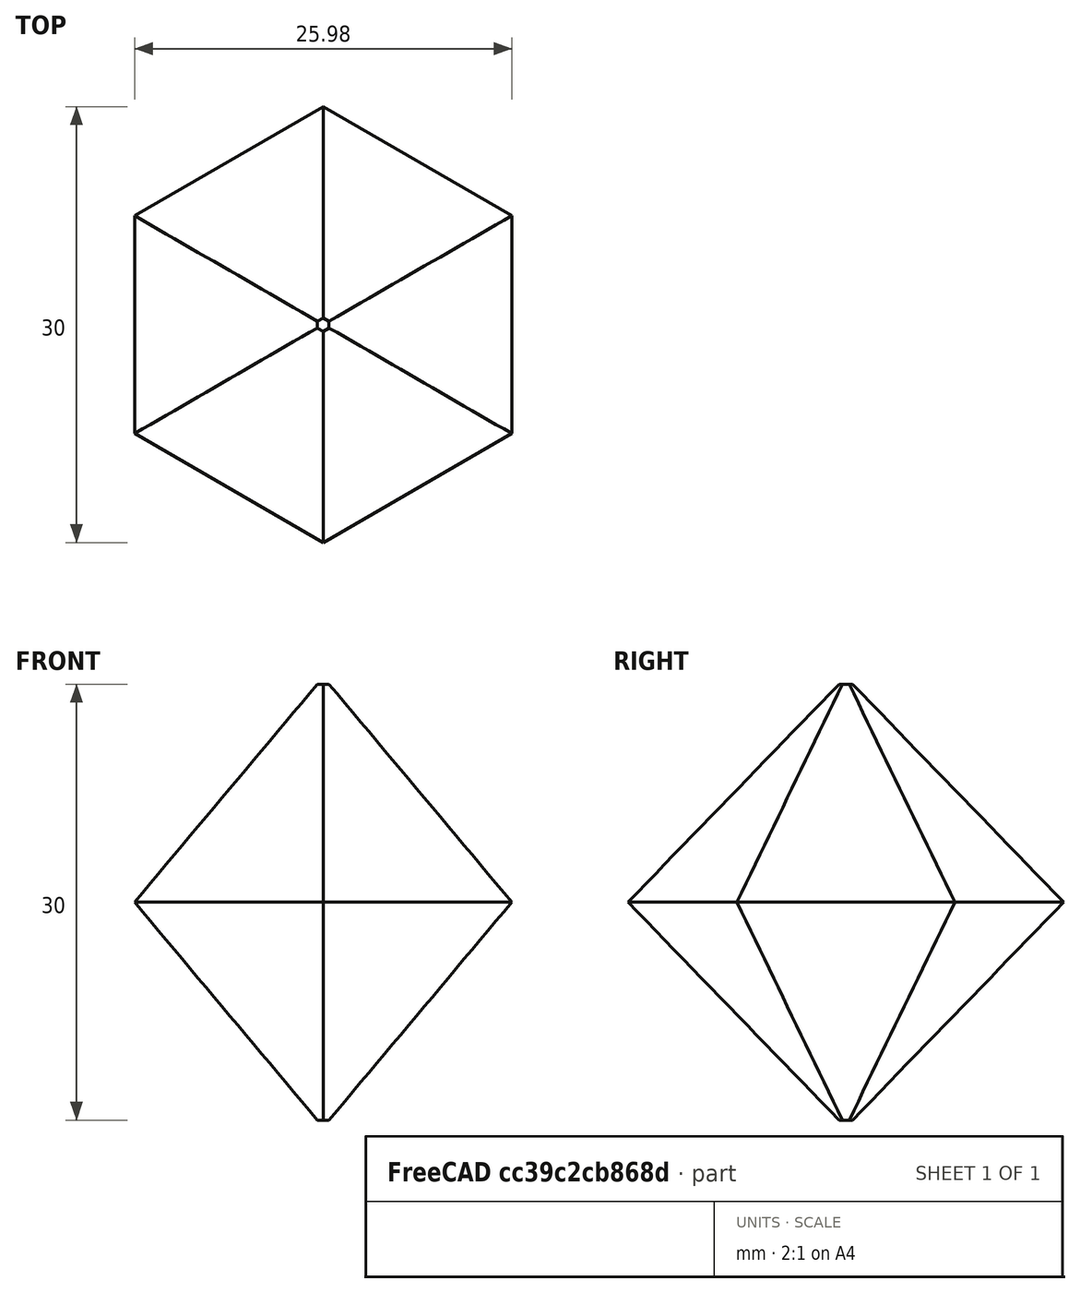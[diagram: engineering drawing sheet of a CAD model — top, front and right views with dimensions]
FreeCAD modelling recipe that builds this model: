
FCSTD DOCUMENT  (FreeCAD 1.1R20260414 (Git shallow))
Label: lesson17
License: All rights reserved
objects: App::Point×1, Sketcher::SketchObject×1, PartDesign::Pad×1, PartDesign::Body×1, App::VarSet×1
note: 6 computed .brp shape members not serialized (recipe doc carries the construction recipe); baked Part::Feature solids carry a one-line shape summary decoded from their .brp

FEATURE [App::Point] Origin001
  Role = Origin
FEATURE [Sketcher::SketchObject] Sketch
  ArcFitTolerance = 1e-06
  AttachmentSupport = -> [Origin]
  ExternalTypes = [0]
  FullyConstrained = true
  MakeInternals = false
  MapMode = 5
  _ExternalGeoVersion = 1
  sketch-geometry (7):
    g0: LineSegment StartX=0 StartY=-15 StartZ=0 EndX=12.9904 EndY=-7.5 EndZ=0
    g1: LineSegment StartX=12.9904 StartY=-7.5 StartZ=0 EndX=12.9904 EndY=7.5 EndZ=0
    g2: LineSegment StartX=12.9904 StartY=7.5 StartZ=0 EndX=-6e-16 EndY=15 EndZ=0
    g3: LineSegment StartX=-6e-16 StartY=15 StartZ=0 EndX=-12.9904 EndY=7.5 EndZ=0
    g4: LineSegment StartX=-12.9904 StartY=7.5 StartZ=0 EndX=-12.9904 EndY=-7.5 EndZ=0
    g5: LineSegment StartX=-12.9904 StartY=-7.5 StartZ=0 EndX=6e-16 EndY=-15 EndZ=0
    g6: Circle [constr] CenterX=0 CenterY=0 CenterZ=0 NormalX=0 NormalY=0 NormalZ=1 AngleXU=0 Radius=15
  constraints (16):
    c: Coincident(g0,g1)
    c: Coincident(g1,g2)
    c: Coincident(g2,g3)
    c: Coincident(g3,g4)
    c: Coincident(g4,g5)
    c: Coincident(g5,g0)
    c: Equal(g0, g1-g5) x5
    c: PointOnObject(g0,g6)
    c: PointOnObject(g1,g6)
    c: PointOnObject(g2,g6)
    c: PointOnObject(g3,g6)
    c: PointOnObject(g4,g6)
    c: PointOnObject(g5,g6)
    c: Coincident(g6,g-1)
    c: PointOnObject(g5,g-2)
    c: Diameter(g6) = 30
FEATURE [PartDesign::Pad] Pad
  Direction = (0,0,1)
  Length = 30
  Length2 = 10
  Profile = -> Sketch
  ReferenceAxis = -> Sketch [N_Axis]
  Refine = true
  SideType = 2
  Suppressed = false
  TaperAngle = -40
  Type = 0
  Type2 = 0
FEATURE [PartDesign::Body] Body
  AllowCompound = true
  Group = -> [Sketch,Pad]
  Origin = -> Origin
  Tip = -> Pad
FEATURE [App::VarSet] VarSet
